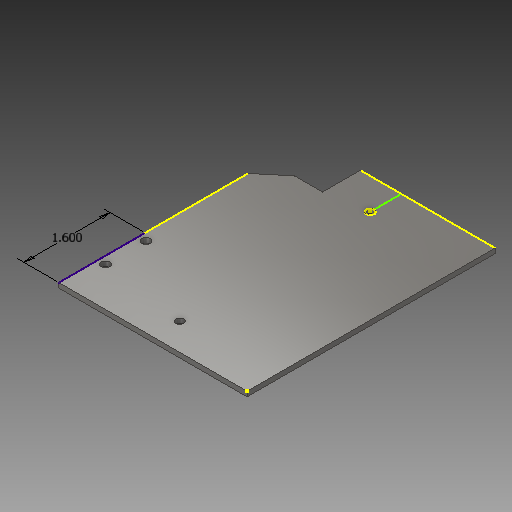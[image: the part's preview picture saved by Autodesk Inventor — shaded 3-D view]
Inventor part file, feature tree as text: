
AUTODESK INVENTOR PART (.ipt)
format: ipt  version: 2017 (Build 210142000, 142)  size: 119,296 bytes
history: native  units: in
note: dims shown in document units (in); Inventor stores cm internally (conversion verified against a paired STEP export)
features: sketch x4, other x4, extrude x2, reference x2
ambient origin geometry x8: Origin, YZ Plane, XZ Plane, XY Plane, X Axis, Y Axis, Z Axis, Center Point
bodies: Solid1 (feature_tree)
feature tree (12):
  extrude  "Extrusion1"  Depth=2.5in
  sketch  "Sketch2"  dims[d2=0.7in d3=0.52in]
  extrude  "Extrusion2"  Depth=0.7in
  sketch  "Sketch4"  dims[d6=3.5in d11=0.09in d12=0.0in d13=1.6in d14=0.75in d15=0.0in]
  sketch  "Sketch1"  dims[d0=4.6in d1=2.5in]
  sketch  "Sketch3"  dims[d4=3.5in]
  reference  "Reference1"
  reference  "Reference2"
  other  "<userpath>\Documents\GitHub\RobotuxCAD\Team Robotux 15-16 Robot Cad Assets\Flywheels.iam"
  other  "Flywheels.iam"
  other  "Flywheel w motor:1"
  other  "am-2875+Banebots+P60+4-1:1"
